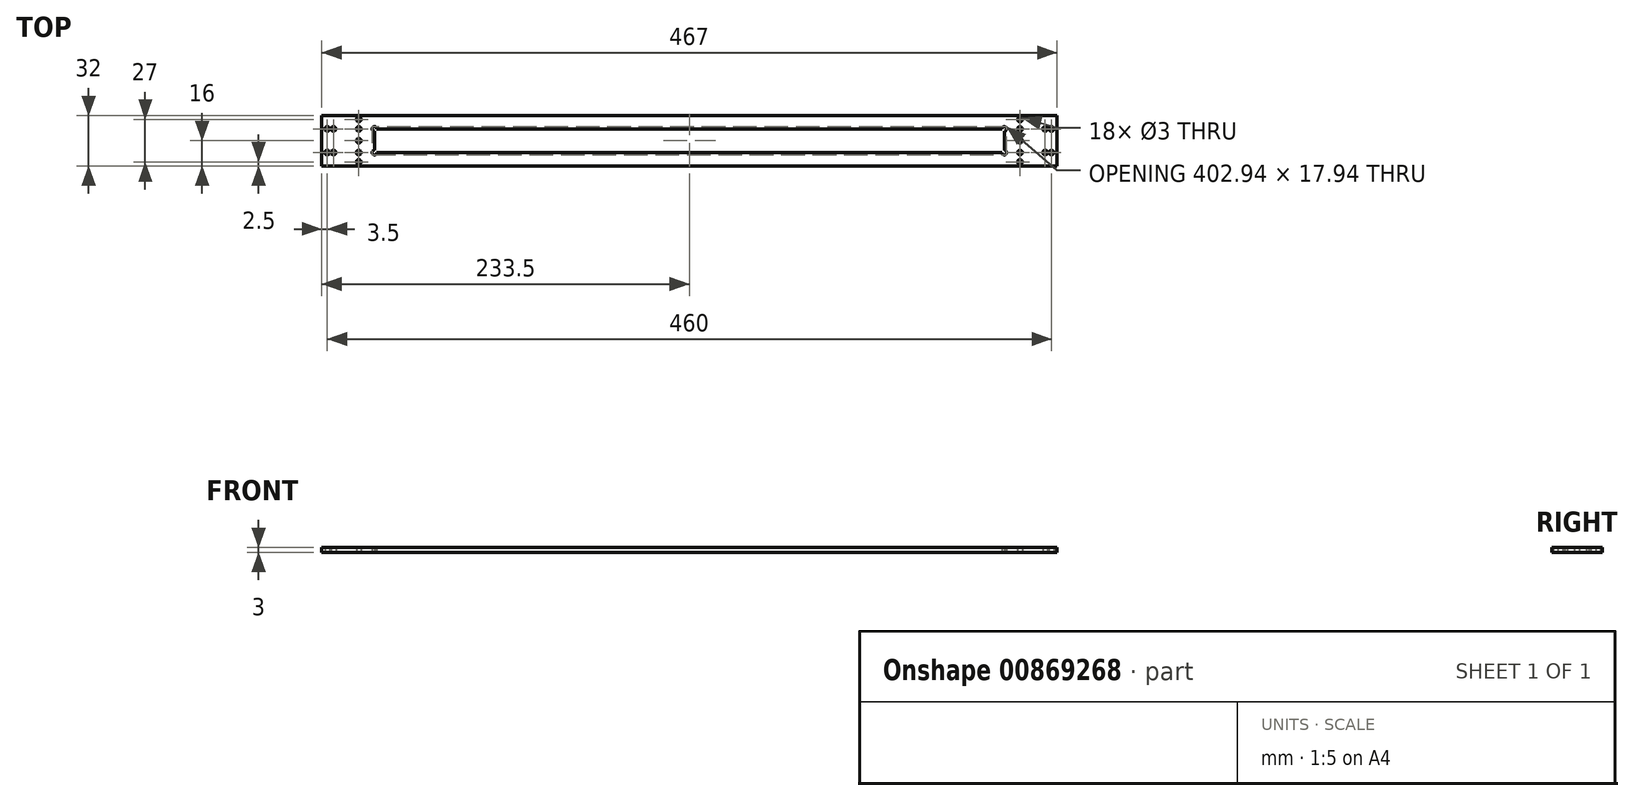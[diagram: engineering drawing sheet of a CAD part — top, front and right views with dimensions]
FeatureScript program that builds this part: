
annotation { "Feature Type Name" : "Feature", "Feature Type Description" : "" }
export const myFeature = defineFeature(function(context is Context, id is Id, definition is map)
    precondition{}
    {
        {
            var Q0;
            Q0=qCreatedBy(makeId("Top.planeOp"),FACE);
            var sketch = newSketch(context, id + "F0", { "sketchPlane" : qUnion([Q0])});
            skLineSegment(sketch, "E0.bottom", {"start": v(233.5, -16) * mm, "end": v(-233.5, -16) * mm});
            skLineSegment(sketch, "E0.top", {"start": v(233.5, 16) * mm, "end": v(-233.5, 16) * mm});
            skLineSegment(sketch, "E0.left", {"start": v(233.5, -16) * mm, "end": v(233.5, 16) * mm});
            skLineSegment(sketch, "E0.right", {"start": v(-233.5, -16) * mm, "end": v(-233.5, 16) * mm});
            skPoint(sketch, "E0.middle", {"position": v(0, 0) * mm});
            skLineSegment(sketch, "E1.bottom", {"start": v(210, -7.5) * mm, "end": v(-210, -7.5) * mm});
            skLineSegment(sketch, "E1.top", {"start": v(210, 7.5) * mm, "end": v(-210, 7.5) * mm});
            skLineSegment(sketch, "E1.left", {"start": v(210, -7.5) * mm, "end": v(210, 7.5) * mm});
            skLineSegment(sketch, "E1.right", {"start": v(-210, -7.5) * mm, "end": v(-210, 7.5) * mm});
            skLineSegment(sketch, "E2.bottom", {"start": v(230, 7.5) * mm, "end": v(-230, 7.5) * mm});
            skLineSegment(sketch, "E2.top", {"start": v(230, -7.5) * mm, "end": v(-230, -7.5) * mm});
            skLineSegment(sketch, "E2.left", {"start": v(230, 7.5) * mm, "end": v(230, -7.5) * mm});
            skLineSegment(sketch, "E2.right", {"start": v(-230, 7.5) * mm, "end": v(-230, -7.5) * mm});
            skPoint(sketch, "E3", {"position": v(210, -7.5) * mm});
            skLineSegment(sketch, "E4", {"start": v(210, -7.5) * mm, "end": v(210, -13.5) * mm});
            skLineSegment(sketch, "E5", {"start": v(210, 7.5) * mm, "end": v(210, 13.5) * mm});
            skLineSegment(sketch, "E6", {"start": v(-210, -7.5) * mm, "end": v(-210, -13.5) * mm});
            skLineSegment(sketch, "E7", {"start": v(-210, 7.5) * mm, "end": v(-210, 13.5) * mm});
            skPoint(sketch, "E7.startSnap0", {"position": v(-210, -10.5) * mm});
            skLineSegment(sketch, "E8", {"start": v(226, 7.5) * mm, "end": v(226, -7.5) * mm});
            skLineSegment(sketch, "E9", {"start": v(-226, 7.5) * mm, "end": v(-226, -7.5) * mm});
            skLineSegment(sketch, "E10.bottom", {"start": v(200, 7.5) * mm, "end": v(-200, 7.5) * mm});
            skLineSegment(sketch, "E10.top", {"start": v(200, -7.5) * mm, "end": v(-200, -7.5) * mm});
            skLineSegment(sketch, "E10.left", {"start": v(200, 7.5) * mm, "end": v(200, -7.5) * mm});
            skLineSegment(sketch, "E10.right", {"start": v(-200, 7.5) * mm, "end": v(-200, -7.5) * mm});
            skPoint(sketch, "E11", {"position": v(210, 0) * mm});
            skPoint(sketch, "E12", {"position": v(-210, 0) * mm});
            skSolve(sketch);
        }
        {
            var Q0;
            {var subQ0=sQuery(id+"F0.wireOp",EDGE,"E1.left");Q0=makeQuery(id+"F0.imprint","IMPRINT",FACE,{"disambiguationData":[TD([[makeQuery(id+"F0.imprint","IMPRINT",EDGE,{"derivedFrom":subQ0}),1.0]])]});}
            var Q1;
            {var subQ0=sQuery(id+"F0.wireOp",EDGE,"E1.left");Q1=makeQuery(id+"F0.imprint","IMPRINT",FACE,{"disambiguationData":[TD([[makeQuery(id+"F0.imprint","IMPRINT",EDGE,{"derivedFrom":subQ0}),-1.0]])]});}
            var Q2;
            Q2=makeQuery(id+"F0.imprint","IMPRINT",FACE,{"disambiguationData":[TD([[makeQuery(id+"F0.imprint","IMPRINT",EDGE,{"derivedFrom":sQuery(id+"F0.wireOp",EDGE,"E0.bottom")}),-1.0]])]});
            var Q3;
            {var subQ0=sQuery(id+"F0.wireOp",EDGE,"E1.right");Q3=makeQuery(id+"F0.imprint","IMPRINT",FACE,{"disambiguationData":[TD([[makeQuery(id+"F0.imprint","IMPRINT",EDGE,{"derivedFrom":subQ0}),1.0]])]});}
            var Q4;
            {var subQ0=sQuery(id+"F0.wireOp",EDGE,"E0.left");Q4=makeQuery(id+"F0.imprint","IMPRINT",FACE,{"disambiguationData":[TD([[makeQuery(id+"F0.imprint","IMPRINT",EDGE,{"derivedFrom":subQ0}),1.0]])]});}
            var Q5;
            {var subQ0=sQuery(id+"F0.wireOp",EDGE,"E5");var subQ1=sQuery(id+"F0.wireOp",EDGE,"E0.top");var subQ2=makeQuery(id+"F0.imprint","INTERSECT",VERTEX,{"derivedFrom":[subQ1,subQ0]});Q5=makeQuery(id+"F0.imprint","IMPRINT",FACE,{"disambiguationData":[TD([[makeQuery(id+"F0.imprint","IMPRINT",EDGE,{"disambiguationData":[TD([[subQ2,-1.0]])],"derivedFrom":subQ1}),1.0]])]});}
            var Q6;
            {var subQ0=sQuery(id+"F0.wireOp",EDGE,"E0.right");Q6=makeQuery(id+"F0.imprint","IMPRINT",FACE,{"disambiguationData":[TD([[makeQuery(id+"F0.imprint","IMPRINT",EDGE,{"derivedFrom":subQ0}),-1.0]])]});}
            var Q7;
            {var subQ0=sQuery(id+"F0.wireOp",EDGE,"E2.right");Q7=makeQuery(id+"F0.imprint","IMPRINT",FACE,{"disambiguationData":[TD([[makeQuery(id+"F0.imprint","IMPRINT",EDGE,{"derivedFrom":subQ0}),1.0]])]});}
            var Q8;
            {var subQ0=sQuery(id+"F0.wireOp",EDGE,"E2.left");Q8=makeQuery(id+"F0.imprint","IMPRINT",FACE,{"disambiguationData":[TD([[makeQuery(id+"F0.imprint","IMPRINT",EDGE,{"derivedFrom":subQ0}),-1.0]])]});}
            var Q9;
            {var subQ0=sQuery(id+"F0.wireOp",EDGE,"E1.right");Q9=makeQuery(id+"F0.imprint","IMPRINT",FACE,{"disambiguationData":[TD([[makeQuery(id+"F0.imprint","IMPRINT",EDGE,{"derivedFrom":subQ0}),-1.0]])]});}
            var Q10;
            Q10=makeQuery(id+"F0.imprint","IMPRINT",FACE,{"disambiguationData":[TD([[makeQuery(id+"F0.imprint","IMPRINT",EDGE,{"derivedFrom":sQuery(id+"F0.wireOp",EDGE,"E10.bottom")}),1.0]])]});
            extrude(context, id + "F1", {"entities" : qUnion([Q0, Q1, Q2, Q3, Q4, Q5, Q6, Q7, Q8, Q9, Q10]), "depth" : 3 * mm, "offsetDistance" : 25 * mm});
        }
        {
            var Q0;
            Q0=sQuery(id+"F0.wireOp",VERTEX,"E1.bottom.start");
            var Q1;
            Q1=sQuery(id+"F0.wireOp",VERTEX,"E1.top.start");
            var Q2;
            Q2=sQuery(id+"F0.wireOp",VERTEX,"E2.bottom.start");
            var Q3;
            Q3=sQuery(id+"F0.wireOp",VERTEX,"E2.top.start");
            var Q4;
            Q4=sQuery(id+"F0.wireOp",VERTEX,"E1.bottom.end");
            var Q5;
            Q5=sQuery(id+"F0.wireOp",VERTEX,"E1.top.end");
            var Q6;
            Q6=sQuery(id+"F0.wireOp",VERTEX,"E2.bottom.end");
            var Q7;
            Q7=sQuery(id+"F0.wireOp",VERTEX,"E2.top.end");
            var Q8;
            Q8=sQuery(id+"F0.wireOp",VERTEX,"E4.end");
            var Q9;
            Q9=sQuery(id+"F0.wireOp",VERTEX,"E6.end");
            var Q10;
            Q10=sQuery(id+"F0.wireOp",VERTEX,"E7.end");
            var Q11;
            Q11=sQuery(id+"F0.wireOp",VERTEX,"E5.end");
            var Q12;
            Q12=sQuery(id+"F0.wireOp",VERTEX,"E8.end");
            var Q13;
            Q13=sQuery(id+"F0.wireOp",VERTEX,"E8.start");
            var Q14;
            Q14=sQuery(id+"F0.wireOp",VERTEX,"E9.end");
            var Q15;
            Q15=sQuery(id+"F0.wireOp",VERTEX,"E9.start");
            var Q16;
            Q16=sQuery(id+"F0.wireOp",VERTEX,"E10.top.start");
            var Q17;
            Q17=sQuery(id+"F0.wireOp",VERTEX,"E10.bottom.start");
            var Q18;
            Q18=sQuery(id+"F0.wireOp",VERTEX,"E10.bottom.end");
            var Q19;
            Q19=sQuery(id+"F0.wireOp",VERTEX,"E10.top.end");
            var Q20;
            Q20=sQuery(id+"F0.wireOp",VERTEX,"E12");
            var Q21;
            Q21=sQuery(id+"F0.wireOp",VERTEX,"E11");
            var Q22;
            Q22=makeQuery(id+"F1.opExtrude","SWEPT_BODY",BODY,{"disambiguationData":[OSD([sQuery(id+"F0.wireOp",EDGE,"E0.bottom"),sQuery(id+"F0.wireOp",EDGE,"E0.top"),sQuery(id+"F0.wireOp",EDGE,"E0.left"),sQuery(id+"F0.wireOp",EDGE,"E0.right"),sQuery(id+"F0.wireOp",EDGE,"E1.right"),sQuery(id+"F0.wireOp",EDGE,"E2.bottom"),sQuery(id+"F0.wireOp",EDGE,"E2.top"),sQuery(id+"F0.wireOp",EDGE,"E2.right")])]});
            hole(context, id + "F2", {"style" : HoleStyle.SIMPLE, "endStyle" : HoleEndStyle.THROUGH, "oppositeDirection" : true, "holeDiameter" : 3 * mm, "majorDiameter" : 5 * mm, "isTappedThrough" : true, "tappedDepth" : 12 * mm, "tapClearance" : 3, "locations" : qUnion([Q0, Q1, Q2, Q3, Q4, Q5, Q6, Q7, Q8, Q9, Q10, Q11, Q12, Q13, Q14, Q15, Q16, Q17, Q18, Q19, Q20, Q21]), "scope" : qUnion([Q22])});
        }
    });
